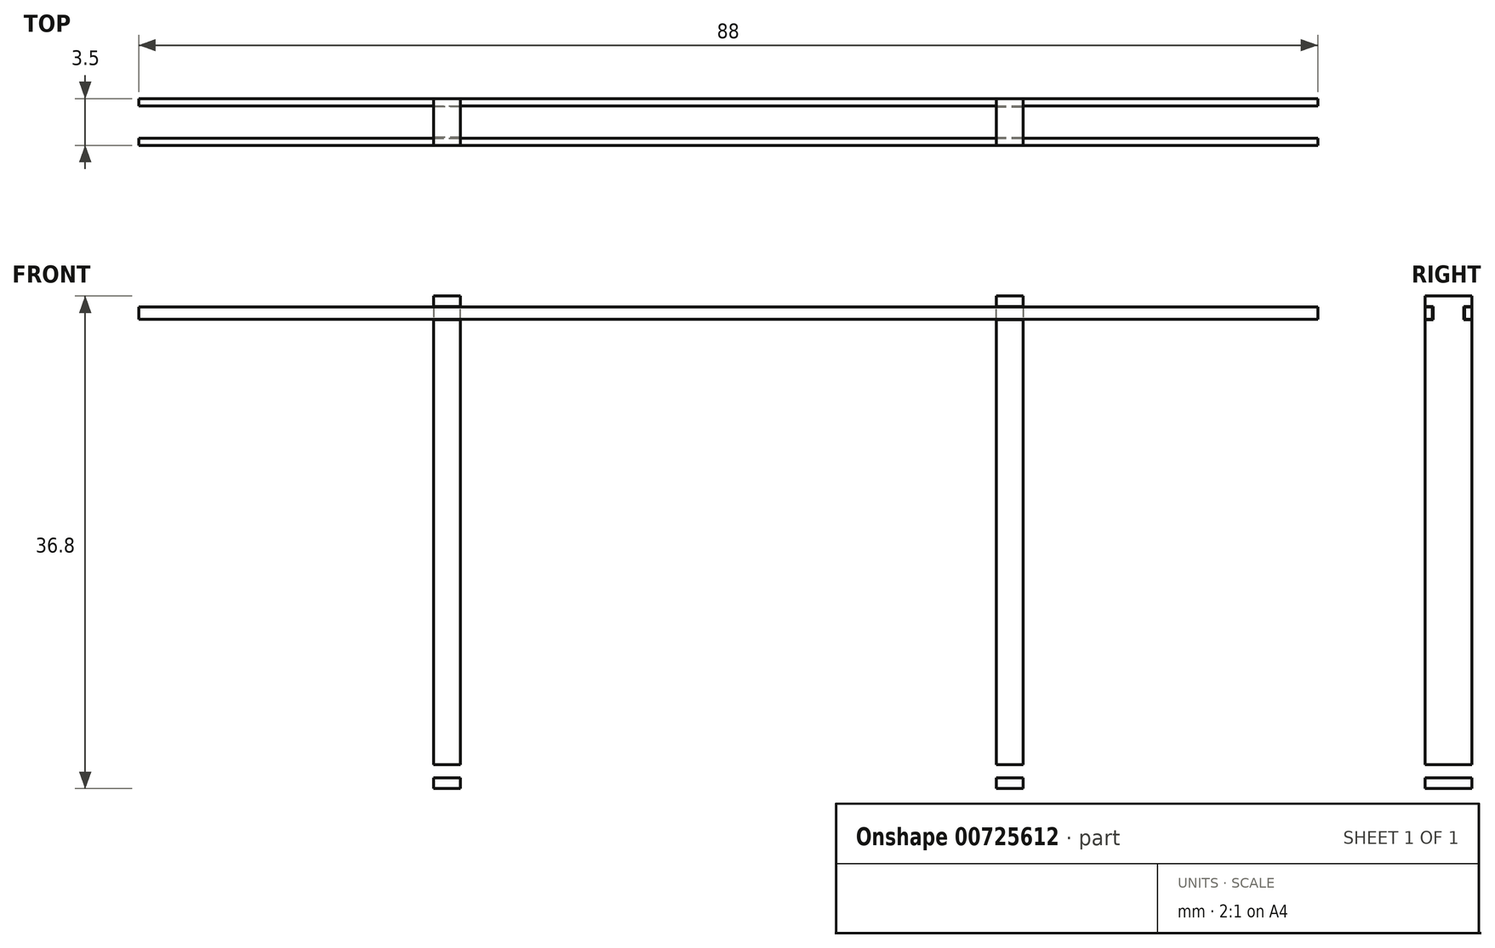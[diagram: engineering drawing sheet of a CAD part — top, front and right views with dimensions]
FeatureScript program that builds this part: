
annotation { "Feature Type Name" : "Feature", "Feature Type Description" : "" }
export const myFeature = defineFeature(function(context is Context, id is Id, definition is map)
    precondition{}
    {
        {
            var Q0;
            Q0=qCreatedBy(makeId("Front.planeOp"),FACE);
            var sketch = newSketch(context, id + "F0", { "sketchPlane" : qUnion([Q0])});
            skCircle(sketch, "E0.0", {"center": v(-4.5, 0) * mm, "radius": 1 * mm, "construction": true});
            skCircle(sketch, "E0.2", {"center": v(4.5, 0) * mm, "radius": 1 * mm, "construction": true});
            skLineSegment(sketch, "E1", {"start": v(-3.5, 0) * mm, "end": v(-3.5, 1.75) * mm});
            skLineSegment(sketch, "E2", {"start": v(3.5, 0) * mm, "end": v(3.5, 1.63) * mm});
            skLineSegment(sketch, "E3", {"start": v(-4.5, 1) * mm, "end": v(4.5, 1) * mm});
            skLineSegment(sketch, "E4", {"start": v(4.5, -1) * mm, "end": v(-4.5, -1) * mm});
            skLineSegment(sketch, "E5", {"start": v(0, 1) * mm, "end": v(0, -1) * mm, "construction": true});
            skLineSegment(sketch, "E6", {"start": v(-4.5, 1) * mm, "end": v(-4.5, -1) * mm});
            skLineSegment(sketch, "E7", {"start": v(4.5, 1) * mm, "end": v(4.5, -1) * mm});
            skLineSegment(sketch, "E8.top", {"start": v(4.5, 1) * mm, "end": v(-4.5, 1) * mm});
            skLineSegment(sketch, "E8.left", {"start": v(4.5, -1) * mm, "end": v(4.5, 1) * mm});
            skLineSegment(sketch, "E8.right", {"start": v(-4.5, -1) * mm, "end": v(-4.5, 1) * mm});
            skPoint(sketch, "E8.middle", {"position": v(0, 0) * mm});
            skLineSegment(sketch, "E9", {"start": v(-6.13, 0) * mm, "end": v(6.15, 0) * mm, "construction": true});
            skLineSegment(sketch, "E10", {"start": v(-4.5, 0) * mm, "end": v(4.5, 0) * mm});
            skLineSegment(sketch, "E11", {"start": v(1, -0.8) * mm, "end": v(-1, -0.8) * mm});
            skPoint(sketch, "E12", {"position": v(-1.7, -1) * mm});
            skLineSegment(sketch, "E13", {"start": v(1, -0.8) * mm, "end": v(1, 36) * mm});
            skLineSegment(sketch, "E14", {"start": v(-1, -0.8) * mm, "end": v(-1, 36) * mm});
            skLineSegment(sketch, "E15", {"start": v(-1, 36) * mm, "end": v(1, 36) * mm});
            skLineSegment(sketch, "E16.bottom", {"start": v(-1, 36) * mm, "end": v(-41, 36) * mm});
            skLineSegment(sketch, "E16.top", {"start": v(-1, 33.82) * mm, "end": v(-41, 33.82) * mm});
            skLineSegment(sketch, "E16.left", {"start": v(-1, 36) * mm, "end": v(-1, 33.82) * mm});
            skLineSegment(sketch, "E16.right", {"start": v(-41, 36) * mm, "end": v(-41, 33.82) * mm});
            skLineSegment(sketch, "E17", {"start": v(0, -0.8) * mm, "end": v(0, 0) * mm, "construction": true});
            skLineSegment(sketch, "E18", {"start": v(-21, 36) * mm, "end": v(-21, -11.56) * mm});
            skLineSegment(sketch, "E19.MirrorCS", {"start": v(-37.5, 1) * mm, "end": v(-37.5, -1) * mm});
            skLineSegment(sketch, "E20.MirrorCS", {"start": v(-46.5, 1) * mm, "end": v(-46.5, -1) * mm});
            skLineSegment(sketch, "E21.MirrorCS", {"start": v(-37.5, -1) * mm, "end": v(-37.5, 1) * mm});
            skLineSegment(sketch, "E22.MirrorCS", {"start": v(-43, -0.8) * mm, "end": v(-41, -0.8) * mm});
            skLineSegment(sketch, "E23.MirrorCS", {"start": v(-46.5, -1) * mm, "end": v(-46.5, 1) * mm});
            skLineSegment(sketch, "E24.MirrorCS", {"start": v(-42, -0.8) * mm, "end": v(-42, 0) * mm, "construction": true});
            skLineSegment(sketch, "E25.MirrorCS", {"start": v(-38.5, 0) * mm, "end": v(-38.5, 1.75) * mm});
            skLineSegment(sketch, "E26.MirrorCS", {"start": v(-35.87, 0) * mm, "end": v(-48.15, 0) * mm, "construction": true});
            skLineSegment(sketch, "E27.MirrorCS", {"start": v(-42, 1) * mm, "end": v(-42, -1) * mm, "construction": true});
            skCircle(sketch, "E28.MirrorC", {"center": v(-37.5, 0) * mm, "radius": 1 * mm, "construction": true});
            skLineSegment(sketch, "E29.MirrorCS", {"start": v(-37.5, 1) * mm, "end": v(-46.5, 1) * mm});
            skLineSegment(sketch, "E30.MirrorCS", {"start": v(-45.5, 0) * mm, "end": v(-45.5, 1.63) * mm});
            skLineSegment(sketch, "E31.MirrorCS", {"start": v(-46.5, -1) * mm, "end": v(-37.5, -1) * mm});
            skCircle(sketch, "E32.MirrorC", {"center": v(-46.5, 0) * mm, "radius": 1 * mm, "construction": true});
            skPoint(sketch, "E33.MirrorP", {"position": v(-42, 0) * mm});
            skPoint(sketch, "E34.MirrorP", {"position": v(-40.3, -1) * mm});
            skLineSegment(sketch, "E35.MirrorCS", {"start": v(-41, 36) * mm, "end": v(-43, 36) * mm});
            skLineSegment(sketch, "E36.MirrorCS", {"start": v(-46.5, 1) * mm, "end": v(-37.5, 1) * mm});
            skLineSegment(sketch, "E37.MirrorCS", {"start": v(-41, -0.8) * mm, "end": v(-41, 36) * mm});
            skLineSegment(sketch, "E38.MirrorCS", {"start": v(-43, -0.8) * mm, "end": v(-43, 36) * mm});
            skLineSegment(sketch, "E39.MirrorCS", {"start": v(-37.5, 0) * mm, "end": v(-46.5, 0) * mm});
            skLineSegment(sketch, "E40", {"start": v(1, 33.93) * mm, "end": v(41, 33.93) * mm, "construction": true});
            skLineSegment(sketch, "E41", {"start": v(21, 33.93) * mm, "end": v(21, 44.06) * mm, "construction": true});
            skLineSegment(sketch, "E42", {"start": v(23, 33.93) * mm, "end": v(23, 38.13) * mm});
            skSolve(sketch);
        }
        {
            var Q0;
            {var subQ5=sQuery(id+"F0.wireOp",EDGE,"E15");Q0=makeQuery(id+"F0.imprint","IMPRINT",FACE,{"disambiguationData":[TD([[makeQuery(id+"F0.imprint","IMPRINT",EDGE,{"derivedFrom":subQ5}),-1.0]])]});}
            var Q1;
            {var subQ0=sQuery(id+"F0.wireOp",EDGE,"E13");var subQ1=sQuery(id+"F0.wireOp",EDGE,"E8.top");var subQ2=makeQuery(id+"F0.imprint","INTERSECT",VERTEX,{"derivedFrom":[subQ1,subQ0]});Q1=makeQuery(id+"F0.imprint","IMPRINT",FACE,{"disambiguationData":[TD([[makeQuery(id+"F0.imprint","IMPRINT",EDGE,{"disambiguationData":[TD([[subQ2,-1.0]])],"derivedFrom":subQ1}),1.0]])]});}
            var Q2;
            {var subQ5=sQuery(id+"F0.wireOp",EDGE,"E11");Q2=makeQuery(id+"F0.imprint","IMPRINT",FACE,{"disambiguationData":[TD([[makeQuery(id+"F0.imprint","IMPRINT",EDGE,{"derivedFrom":subQ5}),-1.0]])]});}
            var Q3;
            {var subQ0=sQuery(id+"F0.wireOp",EDGE,"E16.left");Q3=makeQuery(id+"F0.imprint","IMPRINT",FACE,{"disambiguationData":[TD([[makeQuery(id+"F0.imprint","IMPRINT",EDGE,{"derivedFrom":subQ0}),-1.0]])]});}
            extrude(context, id + "F1", {"entities" : qUnion([Q0, Q1, Q2, Q3]), "endBound" : BoundingType.SYMMETRIC, "depth" : 3.5 * mm, "offsetDistance" : 25 * mm});
        }
        {
            var Q0;
            {var subQ0=sQuery(id+"F0.wireOp",EDGE,"E10");var subQ1=sQuery(id+"F0.wireOp",EDGE,"E2");var subQ2=makeQuery(id+"F0.imprint","INTERSECT",VERTEX,{"derivedFrom":[subQ1,subQ0]});Q0=makeQuery(id+"F0.imprint","IMPRINT",FACE,{"disambiguationData":[TD([[makeQuery(id+"F0.imprint","IMPRINT",EDGE,{"disambiguationData":[TD([[subQ2,-1.0]])],"derivedFrom":subQ1}),1.0]])]});}
            var Q1;
            {var subQ0=sQuery(id+"F0.wireOp",EDGE,"E13");var subQ1=sQuery(id+"F0.wireOp",EDGE,"E8.top");var subQ2=makeQuery(id+"F0.imprint","INTERSECT",VERTEX,{"derivedFrom":[subQ1,subQ0]});Q1=makeQuery(id+"F0.imprint","IMPRINT",FACE,{"disambiguationData":[TD([[makeQuery(id+"F0.imprint","IMPRINT",EDGE,{"disambiguationData":[TD([[subQ2,-1.0]])],"derivedFrom":subQ1}),1.0]])]});}
            var Q2;
            {var subQ0=sQuery(id+"F0.wireOp",EDGE,"E10");var subQ1=sQuery(id+"F0.wireOp",EDGE,"E1");var subQ2=makeQuery(id+"F0.imprint","INTERSECT",VERTEX,{"derivedFrom":[subQ1,subQ0]});Q2=makeQuery(id+"F0.imprint","IMPRINT",FACE,{"disambiguationData":[TD([[makeQuery(id+"F0.imprint","IMPRINT",EDGE,{"disambiguationData":[TD([[subQ2,-1.0]])],"derivedFrom":subQ1}),-1.0]])]});}
            var Q3;
            Q3=sQuery(id+"F0.wireOp",EDGE,"E9");
            revolve(context, id + "F2", {"surfaceOperationType" : NewSurfaceOperationType.NEW, "entities" : qUnion([Q0, Q1, Q2]), "axis" : qUnion([Q3]), "revolveType" : RevolveType.FULL});
        }
        {
            var Q0;
            Q0=makeQuery(id+"F2.opRevolve","SWEPT_BODY",BODY,{"disambiguationData":[OSD([sQuery(id+"F0.wireOp",EDGE,"E1"),sQuery(id+"F0.wireOp",EDGE,"E2"),sQuery(id+"F0.wireOp",EDGE,"E8.top"),sQuery(id+"F0.wireOp",EDGE,"E10")])]});
            var Q1;
            Q1=makeQuery(id+"F1.opExtrude","SWEPT_BODY",BODY,{"disambiguationData":[OSD([sQuery(id+"F0.wireOp",EDGE,"E11"),sQuery(id+"F0.wireOp",EDGE,"E13"),sQuery(id+"F0.wireOp",EDGE,"E14"),sQuery(id+"F0.wireOp",EDGE,"E15")])]});
            booleanBodies(context, id + "F3", {"operationType" : BooleanOperationType.SUBTRACTION, "tools" : qUnion([Q0]), "targets" : qUnion([Q1])});
        }
        {
            var Q0;
            Q0=sQuery(id+"F0.wireOp",EDGE,"E18");
            extrude(context, id + "F4", {"bodyType" : ToolBodyType.SURFACE, "surfaceEntities" : qUnion([Q0]), "endBound" : BoundingType.SYMMETRIC, "depth" : 25 * mm, "offsetDistance" : 25 * mm});
        }
        {
            var Q0;
            Q0=makeQuery(id+"F1.opExtrude","SWEPT_FACE",FACE,{"disambiguationData":[OSD([sQuery(id+"F0.wireOp",EDGE,"E13")])]});
            var sketch = newSketch(context, id + "F5", { "sketchPlane" : qUnion([Q0])});
            skLineSegment(sketch, "E43.0", {"start": v(1.75, -0.8) * mm, "end": v(1.75, 36) * mm});
            skLineSegment(sketch, "E43.1", {"start": v(-1.75, -0.8) * mm, "end": v(-1.75, 36) * mm});
            skLineSegment(sketch, "E43.2", {"start": v(-1.75, 36) * mm, "end": v(1.75, 36) * mm});
            skPoint(sketch, "E44.0", {"position": v(0, 33.82) * mm});
            skLineSegment(sketch, "E45", {"start": v(-1.75, 33.82) * mm, "end": v(1.75, 33.82) * mm});
            skLineSegment(sketch, "E46.bottom", {"start": v(1.75, 35.22) * mm, "end": v(1.15, 35.22) * mm});
            skLineSegment(sketch, "E46.top", {"start": v(1.75, 34.22) * mm, "end": v(1.15, 34.22) * mm});
            skLineSegment(sketch, "E46.left", {"start": v(1.75, 35.22) * mm, "end": v(1.75, 34.22) * mm});
            skLineSegment(sketch, "E46.right", {"start": v(1.15, 35.22) * mm, "end": v(1.15, 34.22) * mm});
            skLineSegment(sketch, "E47", {"start": v(0, 36.86) * mm, "end": v(0, 32.3) * mm, "construction": true});
            skLineSegment(sketch, "E48", {"start": v(1.15, 34.22) * mm, "end": v(1.15, 33.82) * mm, "construction": true});
            skLineSegment(sketch, "E49", {"start": v(1.15, 35.22) * mm, "end": v(1.15, 36) * mm, "construction": true});
            skLineSegment(sketch, "E50.MirrorCS", {"start": v(-1.75, 35.22) * mm, "end": v(-1.15, 35.22) * mm});
            skLineSegment(sketch, "E51.MirrorCS", {"start": v(-1.15, 35.22) * mm, "end": v(-1.15, 34.22) * mm});
            skLineSegment(sketch, "E52.MirrorCS", {"start": v(-1.75, 34.22) * mm, "end": v(-1.15, 34.22) * mm});
            skLineSegment(sketch, "E53.0", {"start": v(1.75, 35.17) * mm, "end": v(1.2, 35.17) * mm});
            skLineSegment(sketch, "E53.2", {"start": v(1.75, 34.27) * mm, "end": v(1.2, 34.27) * mm});
            skLineSegment(sketch, "E53.3", {"start": v(1.2, 35.17) * mm, "end": v(1.2, 34.27) * mm});
            skLineSegment(sketch, "E54.MirrorCS", {"start": v(-1.75, 35.17) * mm, "end": v(-1.2, 35.17) * mm});
            skLineSegment(sketch, "E55.MirrorCS", {"start": v(-1.2, 35.17) * mm, "end": v(-1.2, 34.27) * mm});
            skLineSegment(sketch, "E56.MirrorCS", {"start": v(-1.75, 34.27) * mm, "end": v(-1.2, 34.27) * mm});
            skSolve(sketch);
        }
        {
            var Q0;
            Q0=sQuery(id+"F0.wireOp",EDGE,"E42");
            extrude(context, id + "F6", {"bodyType" : ToolBodyType.SURFACE, "surfaceEntities" : qUnion([Q0]), "depth" : 25 * mm, "offsetDistance" : 25 * mm});
        }
        {
            var Q0;
            {var subQ1=sQuery(id+"F5.wireOp",EDGE,"E46.bottom");Q0=makeQuery(id+"F5.imprint","IMPRINT",FACE,{"disambiguationData":[TD([[makeQuery(id+"F5.imprint","IMPRINT",EDGE,{"derivedFrom":subQ1}),1.0]])]});}
            var Q1;
            {var subQ0=sQuery(id+"F5.wireOp",EDGE,"E53.0");Q1=makeQuery(id+"F5.imprint","IMPRINT",FACE,{"disambiguationData":[TD([[makeQuery(id+"F5.imprint","IMPRINT",EDGE,{"derivedFrom":subQ0}),1.0]])]});}
            var Q2;
            {var subQ0=sQuery(id+"F5.wireOp",EDGE,"E50.MirrorCS");Q2=makeQuery(id+"F5.imprint","IMPRINT",FACE,{"disambiguationData":[TD([[makeQuery(id+"F5.imprint","IMPRINT",EDGE,{"derivedFrom":subQ0}),-1.0]])]});}
            var Q3;
            {var subQ0=sQuery(id+"F5.wireOp",EDGE,"E54.MirrorCS");Q3=makeQuery(id+"F5.imprint","IMPRINT",FACE,{"disambiguationData":[TD([[makeQuery(id+"F5.imprint","IMPRINT",EDGE,{"derivedFrom":subQ0}),-1.0]])]});}
            extrude(context, id + "F7", {"entities" : qUnion([Q0, Q1, Q2, Q3]), "operationType" : NewBodyOperationType.REMOVE, "endBound" : BoundingType.THROUGH_ALL, "oppositeDirection" : true, "depth" : 25 * mm, "offsetDistance" : 25 * mm});
        }
        {
            var Q0;
            {var subQ0=sQuery(id+"F5.wireOp",EDGE,"E53.0");Q0=makeQuery(id+"F5.imprint","IMPRINT",FACE,{"disambiguationData":[TD([[makeQuery(id+"F5.imprint","IMPRINT",EDGE,{"derivedFrom":subQ0}),1.0]])]});}
            var Q1;
            {var subQ0=sQuery(id+"F5.wireOp",EDGE,"E54.MirrorCS");Q1=makeQuery(id+"F5.imprint","IMPRINT",FACE,{"disambiguationData":[TD([[makeQuery(id+"F5.imprint","IMPRINT",EDGE,{"derivedFrom":subQ0}),-1.0]])]});}
            var Q2;
            Q2=makeQuery(id+"F4.opExtrude","SWEPT_FACE",FACE,{"disambiguationData":[OSD([sQuery(id+"F0.wireOp",EDGE,"E18")])]});
            extrude(context, id + "F8", {"entities" : qUnion([Q0, Q1]), "endBound" : BoundingType.UP_TO_SURFACE, "oppositeDirection" : true, "depth" : 25 * mm, "endBoundEntityFace" : qUnion([Q2]), "offsetDistance" : 25 * mm});
        }
        {
            var Q0;
            {var subQ0=sQuery(id+"F5.wireOp",EDGE,"E54.MirrorCS");Q0=makeQuery(id+"F5.imprint","IMPRINT",FACE,{"disambiguationData":[TD([[makeQuery(id+"F5.imprint","IMPRINT",EDGE,{"derivedFrom":subQ0}),-1.0]])]});}
            var Q1;
            {var subQ0=sQuery(id+"F5.wireOp",EDGE,"E53.0");Q1=makeQuery(id+"F5.imprint","IMPRINT",FACE,{"disambiguationData":[TD([[makeQuery(id+"F5.imprint","IMPRINT",EDGE,{"derivedFrom":subQ0}),1.0]])]});}
            var Q2;
            Q2=makeQuery(id+"F6.opExtrude","SWEPT_FACE",FACE,{"disambiguationData":[OSD([sQuery(id+"F0.wireOp",EDGE,"E42")])]});
            extrude(context, id + "F9", {"entities" : qUnion([Q0, Q1]), "operationType" : NewBodyOperationType.ADD, "endBound" : BoundingType.UP_TO_SURFACE, "depth" : 25 * mm, "endBoundEntityFace" : qUnion([Q2]), "offsetDistance" : 25 * mm});
        }
        {
            var Q0;
            Q0=makeQuery(id+"F1.opExtrude","SWEPT_BODY",BODY,{"disambiguationData":[OSD([sQuery(id+"F0.wireOp",EDGE,"E11"),sQuery(id+"F0.wireOp",EDGE,"E13"),sQuery(id+"F0.wireOp",EDGE,"E14"),sQuery(id+"F0.wireOp",EDGE,"E15"),sQuery(id+"F0.wireOp",EDGE,"E16.left")])]});
            var Q1;
            Q1=makeQuery(id+"F8.opExtrude","SWEPT_BODY",BODY,{"disambiguationData":[OSD([sQuery(id+"F5.wireOp",EDGE,"E46.left"),sQuery(id+"F5.wireOp",EDGE,"E53.0"),sQuery(id+"F5.wireOp",EDGE,"E53.2"),sQuery(id+"F5.wireOp",EDGE,"E53.3")])]});
            var Q2;
            Q2=makeQuery(id+"F9.opExtrude","SWEPT_BODY",BODY,{"disambiguationData":[OSD([sQuery(id+"F5.wireOp",EDGE,"E43.1"),sQuery(id+"F5.wireOp",EDGE,"E54.MirrorCS"),sQuery(id+"F5.wireOp",EDGE,"E55.MirrorCS"),sQuery(id+"F5.wireOp",EDGE,"E56.MirrorCS")])]});
            var Q3;
            Q3=makeQuery(id+"F8.opExtrude","SWEPT_BODY",BODY,{"disambiguationData":[OSD([sQuery(id+"F5.wireOp",EDGE,"E43.1"),sQuery(id+"F5.wireOp",EDGE,"E54.MirrorCS"),sQuery(id+"F5.wireOp",EDGE,"E55.MirrorCS"),sQuery(id+"F5.wireOp",EDGE,"E56.MirrorCS")])]});
            var Q4;
            Q4=makeQuery(id+"F4.opExtrude","SWEPT_FACE",FACE,{"disambiguationData":[OSD([sQuery(id+"F0.wireOp",EDGE,"E18")])]});
            mirror(context, id + "F10", {"operationType" : NewBodyOperationType.ADD, "entities" : qUnion([Q0, Q1, Q2, Q3]), "mirrorPlane" : qUnion([Q4])});
        }
        {
            var Q0;
            Q0=makeQuery(id+"F4.opExtrude","SWEPT_BODY",BODY,{"disambiguationData":[OSD([sQuery(id+"F0.wireOp",EDGE,"E18")])]});
            var Q1;
            Q1=makeQuery(id+"F6.opExtrude","SWEPT_BODY",BODY,{"disambiguationData":[OSD([sQuery(id+"F0.wireOp",EDGE,"E42")])]});
            deleteBodies(context, id + "F11", {"entities" : qUnion([Q0, Q1])});
        }
    });
